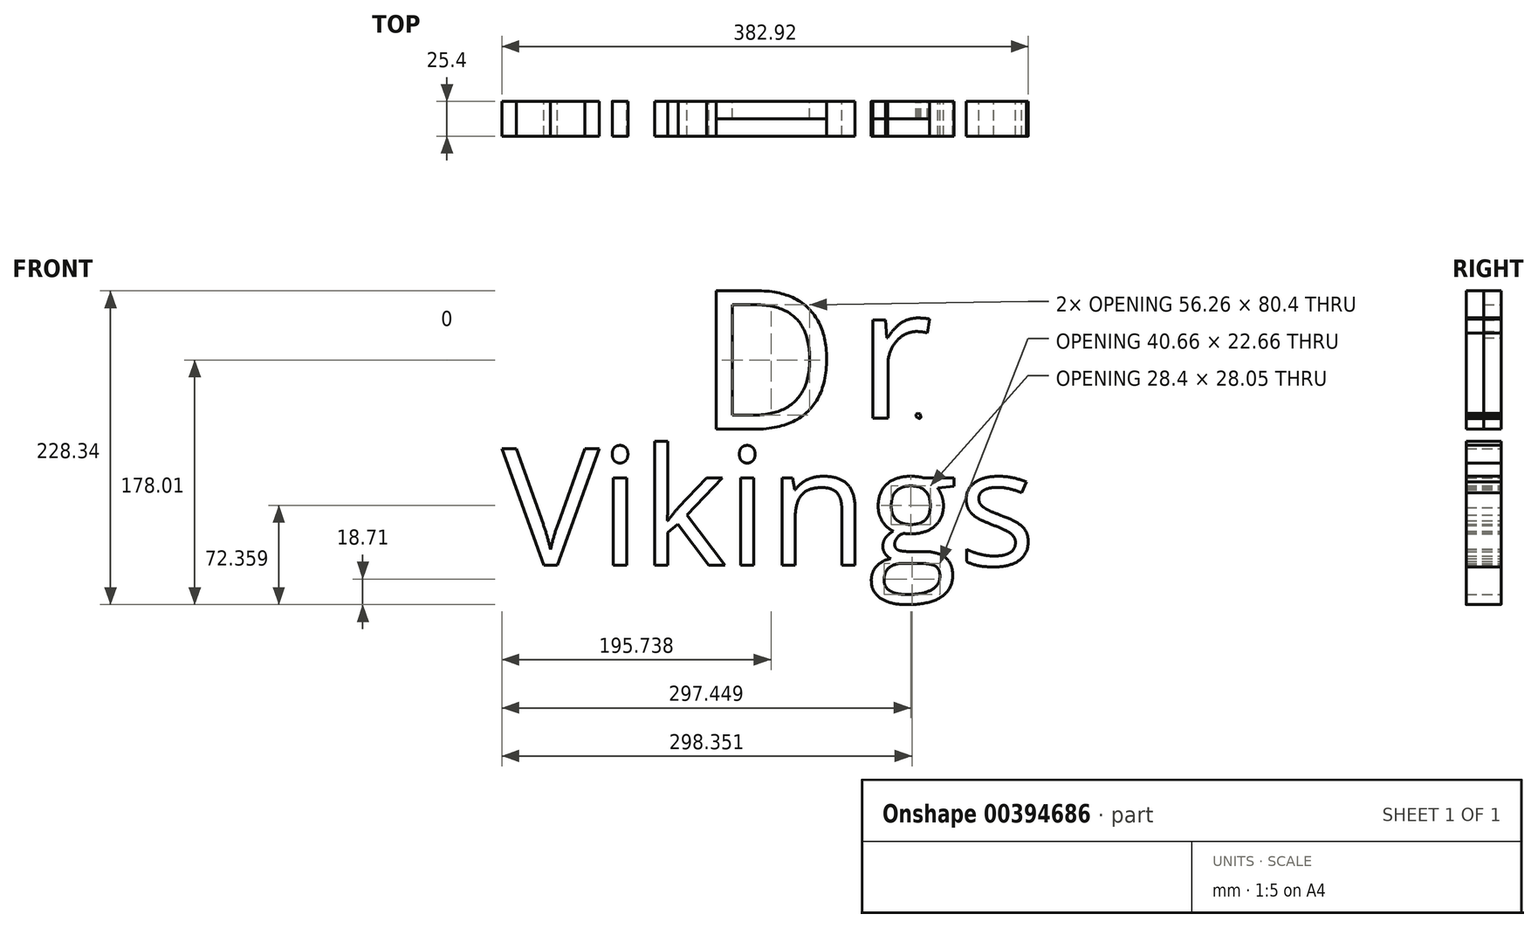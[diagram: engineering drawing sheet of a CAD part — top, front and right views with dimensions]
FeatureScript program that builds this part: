
annotation { "Feature Type Name" : "Feature", "Feature Type Description" : "" }
export const myFeature = defineFeature(function(context is Context, id is Id, definition is map)
    precondition{}
    {
        {
            var Q0;
            Q0=qCreatedBy(makeId("Front.planeOp"),FACE);
            var sketch = newSketch(context, id + "F0", { "sketchPlane" : qUnion([Q0])});
            skText(sketch, "E0", { "text": "D", "fontName": "OpenSans-Regular.ttf"});
            skText(sketch, "E1", { "text": "r", "fontName": "OpenSans-Regular.ttf"});
            skPoint(sketch, "E2", {"position": v(48.16, -7.12) * mm});
            skText(sketch, "E3", { "text": ".", "fontName": "OpenSans-Regular.ttf"});
            skCircle(sketch, "E4.cCircle", {"center": v(40.37, 1.79) * mm, "radius": 1.58 * mm, "construction": true});
            skLineSegment(sketch, "E4.0", {"start": v(42.1, 1.61) * mm, "end": v(41.32, 0.32) * mm});
            skLineSegment(sketch, "E4.1", {"start": v(41.32, 0.32) * mm, "end": v(39.8, 0.13) * mm});
            skLineSegment(sketch, "E4.2", {"start": v(39.8, 0.13) * mm, "end": v(38.72, 1.19) * mm});
            skLineSegment(sketch, "E4.3", {"start": v(38.72, 1.19) * mm, "end": v(38.87, 2.7) * mm});
            skLineSegment(sketch, "E4.4", {"start": v(38.87, 2.7) * mm, "end": v(40.15, 3.52) * mm});
            skLineSegment(sketch, "E4.5", {"start": v(40.15, 3.52) * mm, "end": v(41.59, 3.04) * mm});
            skLineSegment(sketch, "E4.6", {"start": v(41.59, 3.04) * mm, "end": v(42.1, 1.61) * mm});
            skPoint(sketch, "E4.0.midPoint", {"position": v(41.71, 0.96) * mm});
            skPoint(sketch, "E5", {"position": v(38.87, 2.7) * mm});
            const initialGuessF0  = {"E0": [-0.1204, -0.00806, 1, 0, 0.1015], "E1": [-0.00399, 0, 1, 0, 0.09624], "E3": [0.0389, 0, 1, 0, 0.01249]};
            skSetInitialGuess(sketch, initialGuessF0);
            skSolve(sketch);
        }
        {
            var Q0;
            Q0 = qSketchRegion(id + "F0", true);
            extrude(context, id + "F1", {"entities" : qUnion([Q0]), "depth" : 12.7 * mm});
        }
        {
            var Q0;
            Q0=qCreatedBy(makeId("Front.planeOp"),FACE);
            var sketch = newSketch(context, id + "F2", { "sketchPlane" : qUnion([Q0])});
            skText(sketch, "E6", { "text": "Vikings", "fontName": "OpenSans-Regular.ttf"});
            const initialGuessF2  = {"E6": [-0.26248, -0.10717, 1, 0, 0.08566]};
            skSetInitialGuess(sketch, initialGuessF2);
            skSolve(sketch);
        }
        {
            var Q0;
            Q0 = qSketchRegion(id + "F2", true);
            extrude(context, id + "F3", {"entities" : qUnion([Q0]), "depth" : 25.4 * mm});
        }
        {
            var Q0;
            Q0 = qSketchRegion(id + "F0", true);
            extrude(context, id + "F4", {"entities" : qUnion([Q0]), "depth" : 25.4 * mm});
        }
    });
